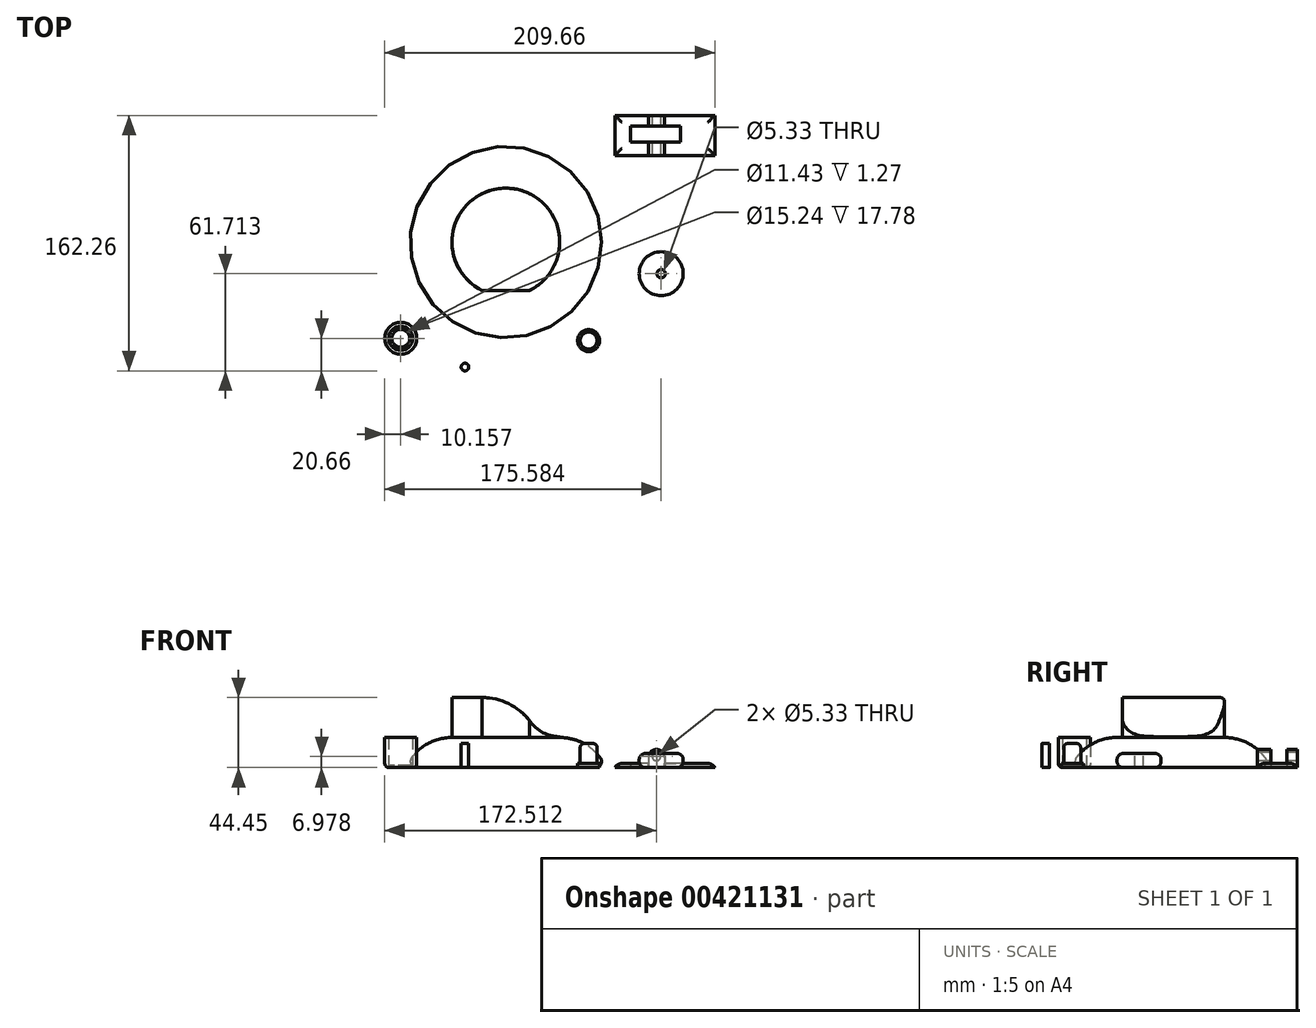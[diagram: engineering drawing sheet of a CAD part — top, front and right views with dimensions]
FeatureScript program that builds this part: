
annotation { "Feature Type Name" : "Feature", "Feature Type Description" : "" }
export const myFeature = defineFeature(function(context is Context, id is Id, definition is map)
    precondition{}
    {
        {
            var Q0;
            Q0=qCreatedBy(makeId("Top.planeOp"),FACE);
            var sketch = newSketch(context, id + "F0", { "sketchPlane" : qUnion([Q0])});
            skCircle(sketch, "E0", {"center": v(0, 0) * mm, "radius": 63.5 * mm});
            skSolve(sketch);
        }
        {
            var Q0;
            Q0=makeQuery(id+"F0.imprint","IMPRINT",FACE,{"disambiguationData":[TD([[makeQuery(id+"F0.imprint","IMPRINT",EDGE,{"derivedFrom":sQuery(id+"F0.wireOp",EDGE,"E0")}),1.0]])]});
            extrude(context, id + "F1", {"entities" : qUnion([Q0]), "depth" : 19.05 * mm});
        }
        {
            var Q0;
            Q0=makeQuery(id+"F1.opExtrude","CAP_EDGE",EDGE,{"disambiguationData":[OSD([sQuery(id+"F0.wireOp",EDGE,"E0")])],"isStart":false});
            fillet(context, id + "F2", {"entities" : qUnion([Q0]), "radius" : 31.75 * mm, "tangentPropagation" : true, "allowEdgeOverflow" : false});
        }
        {
            var Q0;
            {var subQ0=sQuery(id+"F0.wireOp",EDGE,"E0");Q0=makeQuery(id+"F2.opFillet","BLEND_EDGE",EDGE,{"blendedFrom":[makeQuery(id+"F1.opExtrude","CAP_EDGE",EDGE,{"disambiguationData":[OSD([subQ0])],"isStart":false}),makeQuery(id+"F1.opExtrude","CAP_FACE",FACE,{"disambiguationData":[OSD([subQ0])],"isStart":true})],"blendedInto":[makeQuery(id+"F1.opExtrude","CAP_FACE",FACE,{"disambiguationData":[OSD([subQ0])],"isStart":true})]});}
            fillet(context, id + "F3", {"entities" : qUnion([Q0]), "radius" : 3.8 * mm, "tangentPropagation" : true, "allowEdgeOverflow" : false});
        }
        {
            var Q0;
            Q0=makeQuery(id+"F1.opExtrude","CAP_FACE",FACE,{"disambiguationData":[OSD([sQuery(id+"F0.wireOp",EDGE,"E0")])],"isStart":false});
            var sketch = newSketch(context, id + "F4", { "sketchPlane" : qUnion([Q0])});
            skCircle(sketch, "E1", {"center": v(0, 0) * mm, "radius": 34.22 * mm});
            skSolve(sketch);
        }
        {
            var Q0;
            Q0=makeQuery(id+"F4.imprint","IMPRINT",FACE,{"disambiguationData":[TD([[makeQuery(id+"F4.imprint","IMPRINT",EDGE,{"derivedFrom":sQuery(id+"F4.wireOp",EDGE,"E1")}),1.0]])]});
            extrude(context, id + "F5", {"entities" : qUnion([Q0]), "operationType" : NewBodyOperationType.ADD, "depth" : 25.4 * mm});
        }
        {
            var Q0;
            Q0=qCreatedBy(makeId("Front.planeOp"),FACE);
            var sketch = newSketch(context, id + "F6", { "sketchPlane" : qUnion([Q0])});
            skCircle(sketch, "E2", {"center": v(34.2, 42.56) * mm, "radius": 23.03 * mm});
            skSolve(sketch);
        }
        {
            var Q0;
            Q0 = qSketchRegion(id + "F6", true);
            extrude(context, id + "F7", {"entities" : qUnion([Q0]), "operationType" : NewBodyOperationType.REMOVE, "endBound" : BoundingType.THROUGH_ALL, "depth" : 25.4 * mm});
        }
        {
            var Q0;
            Q0=makeQuery(id+"F6.imprint","IMPRINT",FACE,{"disambiguationData":[TD([[makeQuery(id+"F6.imprint","IMPRINT",EDGE,{"derivedFrom":sQuery(id+"F6.wireOp",EDGE,"E2")}),1.0]])]});
            extrude(context, id + "F8", {"entities" : qUnion([Q0]), "operationType" : NewBodyOperationType.REMOVE, "oppositeDirection" : true, "depth" : 71.37 * mm});
        }
        {
            var Q0;
            Q0=makeQuery(id+"F8.boolean.opBoolean","INTERSECT",EDGE,{"derivedFrom":[makeQuery(id+"F5.opExtrude","CAP_FACE",FACE,{"disambiguationData":[OSD([sQuery(id+"F4.wireOp",EDGE,"E1")])],"isStart":false}),makeQuery(id+"F8.opExtrude","SWEPT_FACE",FACE,{"disambiguationData":[OSD([sQuery(id+"F6.wireOp",EDGE,"E2")])]})]});
            fillet(context, id + "F9", {"entities" : qUnion([Q0]), "radius" : 38.1 * mm, "tangentPropagation" : true, "allowEdgeOverflow" : false});
        }
        {
            var Q0;
            Q0=qCreatedBy(makeId("Top.planeOp"),FACE);
            var sketch = newSketch(context, id + "F10", { "sketchPlane" : qUnion([Q0])});
            skCircle(sketch, "E3", {"center": v(-66.75, -61.17) * mm, "radius": 7.62 * mm});
            skCircle(sketch, "E4", {"center": v(-66.75, -61.17) * mm, "radius": 10.16 * mm});
            skCircle(sketch, "E5", {"center": v(-66.75, -61.17) * mm, "radius": 5.71 * mm});
            skSolve(sketch);
        }
        {
            var Q0;
            Q0=makeQuery(id+"F10.imprint","IMPRINT",FACE,{"disambiguationData":[TD([[makeQuery(id+"F10.imprint","IMPRINT",EDGE,{"derivedFrom":sQuery(id+"F10.wireOp",EDGE,"E3")}),1.0]])]});
            extrude(context, id + "F11", {"entities" : qUnion([Q0]), "depth" : 1.27 * mm});
        }
        {
            var Q0;
            Q0=makeQuery(id+"F10.imprint","IMPRINT",FACE,{"disambiguationData":[TD([[makeQuery(id+"F10.imprint","IMPRINT",EDGE,{"derivedFrom":sQuery(id+"F10.wireOp",EDGE,"E3")}),-1.0]])]});
            extrude(context, id + "F12", {"entities" : qUnion([Q0]), "operationType" : NewBodyOperationType.ADD, "depth" : 19.05 * mm});
        }
        {
            var Q0;
            Q0=makeQuery(id+"F12.opExtrude","CAP_EDGE",EDGE,{"disambiguationData":[OSD([sQuery(id+"F10.wireOp",EDGE,"E4")])],"isStart":true});
            fillet(context, id + "F13", {"entities" : qUnion([Q0]), "radius" : 2.54 * mm, "tangentPropagation" : true, "allowEdgeOverflow" : false});
        }
        {
            var Q0;
            Q0=qCreatedBy(makeId("Top.planeOp"),FACE);
            var sketch = newSketch(context, id + "F14", { "sketchPlane" : qUnion([Q0])});
            skCircle(sketch, "E6", {"center": v(52.55, -62.59) * mm, "radius": 6.99 * mm});
            skSolve(sketch);
        }
        {
            var Q0;
            Q0 = qSketchRegion(id + "F14", true);
            extrude(context, id + "F15", {"entities" : qUnion([Q0]), "depth" : 2.54 * mm});
        }
        {
            var Q0;
            Q0=makeQuery(id+"F15.opExtrude","CAP_FACE",FACE,{"disambiguationData":[OSD([sQuery(id+"F14.wireOp",EDGE,"E6")])],"isStart":false});
            var sketch = newSketch(context, id + "F16", { "sketchPlane" : qUnion([Q0])});
            skCircle(sketch, "E7", {"center": v(52.55, -62.59) * mm, "radius": 5.4 * mm});
            skSolve(sketch);
        }
        {
            var Q0;
            Q0=makeQuery(id+"F16.imprint","IMPRINT",FACE,{"disambiguationData":[TD([[makeQuery(id+"F16.imprint","IMPRINT",EDGE,{"derivedFrom":sQuery(id+"F16.wireOp",EDGE,"E7")}),1.0]])]});
            extrude(context, id + "F17", {"entities" : qUnion([Q0]), "operationType" : NewBodyOperationType.ADD, "depth" : 12.7 * mm});
        }
        {
            var Q0;
            Q0=makeQuery(id+"F17.opExtrude","CAP_EDGE",EDGE,{"disambiguationData":[OSD([sQuery(id+"F16.wireOp",EDGE,"E7")])],"isStart":false});
            fillet(context, id + "F18", {"entities" : qUnion([Q0]), "radius" : 2.54 * mm, "tangentPropagation" : true, "allowEdgeOverflow" : false});
        }
        {
            var Q0;
            Q0=makeQuery(id+"F5.opExtrude","CAP_FACE",FACE,{"disambiguationData":[OSD([sQuery(id+"F4.wireOp",EDGE,"E1")])],"isStart":false});
            var sketch = newSketch(context, id + "F19", { "sketchPlane" : qUnion([Q0])});
            skLineSegment(sketch, "E8.bottom", {"start": v(-15.06, -30.74) * mm, "end": v(15.23, -30.74) * mm});
            skLineSegment(sketch, "E8.top", {"start": v(-15.06, -34.89) * mm, "end": v(15.23, -34.89) * mm});
            skLineSegment(sketch, "E8.left", {"start": v(-15.06, -30.74) * mm, "end": v(-15.06, -34.89) * mm});
            skLineSegment(sketch, "E8.right", {"start": v(15.23, -30.74) * mm, "end": v(15.23, -34.89) * mm});
            skSolve(sketch);
        }
        {
            var Q0;
            Q0=makeQuery(id+"F19.imprint","IMPRINT",FACE,{"disambiguationData":[TD([[makeQuery(id+"F19.imprint","IMPRINT",EDGE,{"derivedFrom":sQuery(id+"F19.wireOp",EDGE,"E8.bottom")}),-1.0]])]});
            extrude(context, id + "F20", {"entities" : qUnion([Q0]), "operationType" : NewBodyOperationType.REMOVE, "oppositeDirection" : true, "depth" : 25.4 * mm});
        }
        {
            var Q0;
            Q0=qCreatedBy(makeId("Top.planeOp"),FACE);
            var sketch = newSketch(context, id + "F21", { "sketchPlane" : qUnion([Q0])});
            skLineSegment(sketch, "E9.bottom", {"start": v(69.25, 55.03) * mm, "end": v(132.75, 55.03) * mm});
            skLineSegment(sketch, "E9.top", {"start": v(69.25, 80.43) * mm, "end": v(132.75, 80.43) * mm});
            skLineSegment(sketch, "E9.left", {"start": v(69.25, 55.03) * mm, "end": v(69.25, 80.43) * mm});
            skLineSegment(sketch, "E9.right", {"start": v(132.75, 55.03) * mm, "end": v(132.75, 80.43) * mm});
            skLineSegment(sketch, "E10.bottom", {"start": v(79.08, 63.6) * mm, "end": v(110.83, 63.6) * mm});
            skLineSegment(sketch, "E10.top", {"start": v(79.08, 73.77) * mm, "end": v(110.83, 73.77) * mm});
            skLineSegment(sketch, "E10.left", {"start": v(79.08, 63.6) * mm, "end": v(79.08, 73.77) * mm});
            skLineSegment(sketch, "E10.right", {"start": v(110.83, 63.6) * mm, "end": v(110.83, 73.77) * mm});
            skCircle(sketch, "E11", {"center": v(98.67, -20.12) * mm, "radius": 13.97 * mm});
            skSolve(sketch);
        }
        {
            var Q0;
            Q0=makeQuery(id+"F21.imprint","IMPRINT",FACE,{"disambiguationData":[TD([[makeQuery(id+"F21.imprint","IMPRINT",EDGE,{"derivedFrom":sQuery(id+"F21.wireOp",EDGE,"E9.bottom")}),1.0]])]});
            extrude(context, id + "F22", {"entities" : qUnion([Q0]), "depth" : 2.54 * mm});
        }
        {
            var Q0;
            Q0=makeQuery(id+"F22.opExtrude","CAP_FACE",FACE,{"disambiguationData":[OSD([sQuery(id+"F21.wireOp",EDGE,"E9.bottom"),sQuery(id+"F21.wireOp",EDGE,"E9.top"),sQuery(id+"F21.wireOp",EDGE,"E9.left"),sQuery(id+"F21.wireOp",EDGE,"E9.right"),sQuery(id+"F21.wireOp",EDGE,"E10.bottom"),sQuery(id+"F21.wireOp",EDGE,"E10.top"),sQuery(id+"F21.wireOp",EDGE,"E10.left"),sQuery(id+"F21.wireOp",EDGE,"E10.right")])],"isStart":false});
            var sketch = newSketch(context, id + "F23", { "sketchPlane" : qUnion([Q0])});
            skLineSegment(sketch, "E12.bottom", {"start": v(90.54, 55.03) * mm, "end": v(100.7, 55.03) * mm});
            skLineSegment(sketch, "E12.top", {"start": v(90.54, 63.6) * mm, "end": v(100.7, 63.6) * mm});
            skLineSegment(sketch, "E12.left", {"start": v(90.54, 55.03) * mm, "end": v(90.54, 63.6) * mm});
            skLineSegment(sketch, "E12.right", {"start": v(100.7, 55.03) * mm, "end": v(100.7, 63.6) * mm});
            skLineSegment(sketch, "E13.bottom", {"start": v(90.54, 73.77) * mm, "end": v(100.7, 73.77) * mm});
            skLineSegment(sketch, "E13.top", {"start": v(90.54, 80.43) * mm, "end": v(100.7, 80.43) * mm});
            skLineSegment(sketch, "E13.left", {"start": v(90.54, 73.77) * mm, "end": v(90.54, 80.43) * mm});
            skLineSegment(sketch, "E13.right", {"start": v(100.7, 73.77) * mm, "end": v(100.7, 80.43) * mm});
            skSolve(sketch);
        }
        {
            var Q0;
            Q0 = qSketchRegion(id + "F23", true);
            extrude(context, id + "F24", {"entities" : qUnion([Q0]), "operationType" : NewBodyOperationType.ADD, "depth" : 8.9 * mm});
        }
        {
            var Q0;
            Q0=makeQuery(id+"F24.opExtrude","CAP_EDGE",EDGE,{"disambiguationData":[OSD([sQuery(id+"F23.wireOp",EDGE,"E13.left")])],"isStart":false});
            var Q1;
            Q1=makeQuery(id+"F24.opExtrude","CAP_EDGE",EDGE,{"disambiguationData":[OSD([sQuery(id+"F23.wireOp",EDGE,"E12.left")])],"isStart":false});
            fillet(context, id + "F25", {"entities" : qUnion([Q0, Q1]), "radius" : 5.08 * mm, "tangentPropagation" : true, "allowEdgeOverflow" : false});
        }
        {
            var Q0;
            Q0=makeQuery(id+"F24.opExtrude","CAP_EDGE",EDGE,{"disambiguationData":[OSD([sQuery(id+"F23.wireOp",EDGE,"E12.right")])],"isStart":false});
            var Q1;
            Q1=makeQuery(id+"F24.opExtrude","CAP_EDGE",EDGE,{"disambiguationData":[OSD([sQuery(id+"F23.wireOp",EDGE,"E13.right")])],"isStart":false});
            fillet(context, id + "F26", {"entities" : qUnion([Q0, Q1]), "radius" : 5.08 * mm, "tangentPropagation" : true, "allowEdgeOverflow" : false});
        }
        {
            var Q0;
            Q0=makeQuery(id+"F24.boolean.opBoolean","MERGE",FACE,{"derivedFrom":[makeQuery(id+"F22.opExtrude","SWEPT_FACE",FACE,{"disambiguationData":[OSD([sQuery(id+"F21.wireOp",EDGE,"E9.bottom")])]}),makeQuery(id+"F24.opExtrude","SWEPT_FACE",FACE,{"disambiguationData":[OSD([sQuery(id+"F23.wireOp",EDGE,"E12.bottom")])]})]});
            var sketch = newSketch(context, id + "F27", { "sketchPlane" : qUnion([Q0])});
            skSolve(sketch);
        }
        {
            var Q0;
            {var subQ4=sQuery(id+"F21.wireOp",EDGE,"E9.bottom");Q0=makeQuery(id+"F27.imprint","IMPRINT",FACE,{"disambiguationData":[TD([[makeQuery(id+"F27.imprint","IMPRINT",EDGE,{"derivedFrom":makeQuery(id+"F22.opExtrude","CAP_EDGE",EDGE,{"disambiguationData":[OSD([subQ4])],"isStart":true})}),1.0]])]});}
            var sketch = newSketch(context, id + "F28", { "sketchPlane" : qUnion([Q0])});
            skCircle(sketch, "E14", {"center": v(95.6, 6.98) * mm, "radius": 2.67 * mm});
            skSolve(sketch);
        }
        {
            var Q0;
            Q0 = qSketchRegion(id + "F28", true);
            extrude(context, id + "F29", {"entities" : qUnion([Q0]), "operationType" : NewBodyOperationType.REMOVE, "oppositeDirection" : true, "depth" : 150.11 * mm});
        }
        {
            var Q0;
            {var subQ0=sQuery(id+"F21.wireOp",EDGE,"E9.right");var subQ1=sQuery(id+"F21.wireOp",EDGE,"E9.top");Q0=makeQuery(id+"F24.boolean.opBoolean","SPLIT",EDGE,{"disambiguationData":[TD([makeQuery(id+"F22.opExtrude","SWEPT_FACE",FACE,{"disambiguationData":[OSD([subQ0])]})])],"derivedFrom":makeQuery(id+"F22.opExtrude","CAP_EDGE",EDGE,{"disambiguationData":[OSD([subQ1])],"isStart":false})});}
            var Q1;
            {var subQ0=sQuery(id+"F21.wireOp",EDGE,"E9.right");var subQ1=sQuery(id+"F21.wireOp",EDGE,"E9.bottom");Q1=makeQuery(id+"F24.boolean.opBoolean","SPLIT",EDGE,{"disambiguationData":[TD([makeQuery(id+"F22.opExtrude","SWEPT_FACE",FACE,{"disambiguationData":[OSD([subQ0])]})])],"derivedFrom":makeQuery(id+"F22.opExtrude","CAP_EDGE",EDGE,{"disambiguationData":[OSD([subQ1])],"isStart":false})});}
            var Q2;
            Q2=makeQuery(id+"F22.opExtrude","CAP_EDGE",EDGE,{"disambiguationData":[OSD([sQuery(id+"F21.wireOp",EDGE,"E9.right")])],"isStart":false});
            var Q3;
            {var subQ0=sQuery(id+"F21.wireOp",EDGE,"E9.left");var subQ1=sQuery(id+"F21.wireOp",EDGE,"E9.top");Q3=makeQuery(id+"F24.boolean.opBoolean","SPLIT",EDGE,{"disambiguationData":[TD([makeQuery(id+"F22.opExtrude","SWEPT_FACE",FACE,{"disambiguationData":[OSD([subQ0])]})])],"derivedFrom":makeQuery(id+"F22.opExtrude","CAP_EDGE",EDGE,{"disambiguationData":[OSD([subQ1])],"isStart":false})});}
            var Q4;
            Q4=makeQuery(id+"F22.opExtrude","CAP_EDGE",EDGE,{"disambiguationData":[OSD([sQuery(id+"F21.wireOp",EDGE,"E9.left")])],"isStart":false});
            var Q5;
            {var subQ0=sQuery(id+"F21.wireOp",EDGE,"E9.left");var subQ1=sQuery(id+"F21.wireOp",EDGE,"E9.bottom");Q5=makeQuery(id+"F24.boolean.opBoolean","SPLIT",EDGE,{"disambiguationData":[TD([makeQuery(id+"F22.opExtrude","SWEPT_FACE",FACE,{"disambiguationData":[OSD([subQ0])]})])],"derivedFrom":makeQuery(id+"F22.opExtrude","CAP_EDGE",EDGE,{"disambiguationData":[OSD([subQ1])],"isStart":false})});}
            fillet(context, id + "F30", {"entities" : qUnion([Q0, Q1, Q2, Q3, Q4, Q5]), "radius" : 5.08 * mm, "tangentPropagation" : true, "allowEdgeOverflow" : false});
        }
        {
            var Q0;
            Q0=makeQuery(id+"F21.imprint","IMPRINT",FACE,{"disambiguationData":[TD([[makeQuery(id+"F21.imprint","IMPRINT",EDGE,{"derivedFrom":sQuery(id+"F21.wireOp",EDGE,"E11")}),1.0]])]});
            extrude(context, id + "F31", {"entities" : qUnion([Q0]), "depth" : 8.9 * mm});
        }
        {
            var Q0;
            Q0=makeQuery(id+"F31.opExtrude","CAP_EDGE",EDGE,{"disambiguationData":[OSD([sQuery(id+"F21.wireOp",EDGE,"E11")])],"isStart":true});
            var Q1;
            Q1=makeQuery(id+"F31.opExtrude","CAP_EDGE",EDGE,{"disambiguationData":[OSD([sQuery(id+"F21.wireOp",EDGE,"E11")])],"isStart":false});
            fillet(context, id + "F32", {"entities" : qUnion([Q0, Q1]), "radius" : 3.8 * mm, "tangentPropagation" : true, "allowEdgeOverflow" : false});
        }
        {
            var Q0;
            Q0=makeQuery(id+"F31.opExtrude","CAP_FACE",FACE,{"disambiguationData":[OSD([sQuery(id+"F21.wireOp",EDGE,"E11")])],"isStart":false});
            var sketch = newSketch(context, id + "F33", { "sketchPlane" : qUnion([Q0])});
            skCircle(sketch, "E15", {"center": v(98.67, -20.12) * mm, "radius": 2.67 * mm});
            skSolve(sketch);
        }
        {
            var Q0;
            Q0 = qSketchRegion(id + "F33", true);
            extrude(context, id + "F34", {"entities" : qUnion([Q0]), "operationType" : NewBodyOperationType.REMOVE, "oppositeDirection" : true, "depth" : 29.46 * mm});
        }
        {
            var Q0;
            Q0=qCreatedBy(makeId("Top.planeOp"),FACE);
            var sketch = newSketch(context, id + "F35", { "sketchPlane" : qUnion([Q0])});
            skCircle(sketch, "E16", {"center": v(-25.96, -79.42) * mm, "radius": 2.41 * mm});
            skSolve(sketch);
        }
        {
            var Q0;
            Q0=makeQuery(id+"F35.imprint","IMPRINT",FACE,{"disambiguationData":[TD([[makeQuery(id+"F35.imprint","IMPRINT",EDGE,{"derivedFrom":sQuery(id+"F35.wireOp",EDGE,"E16")}),1.0]])]});
            extrude(context, id + "F36", {"entities" : qUnion([Q0]), "depth" : 15.24 * mm});
        }
    });
